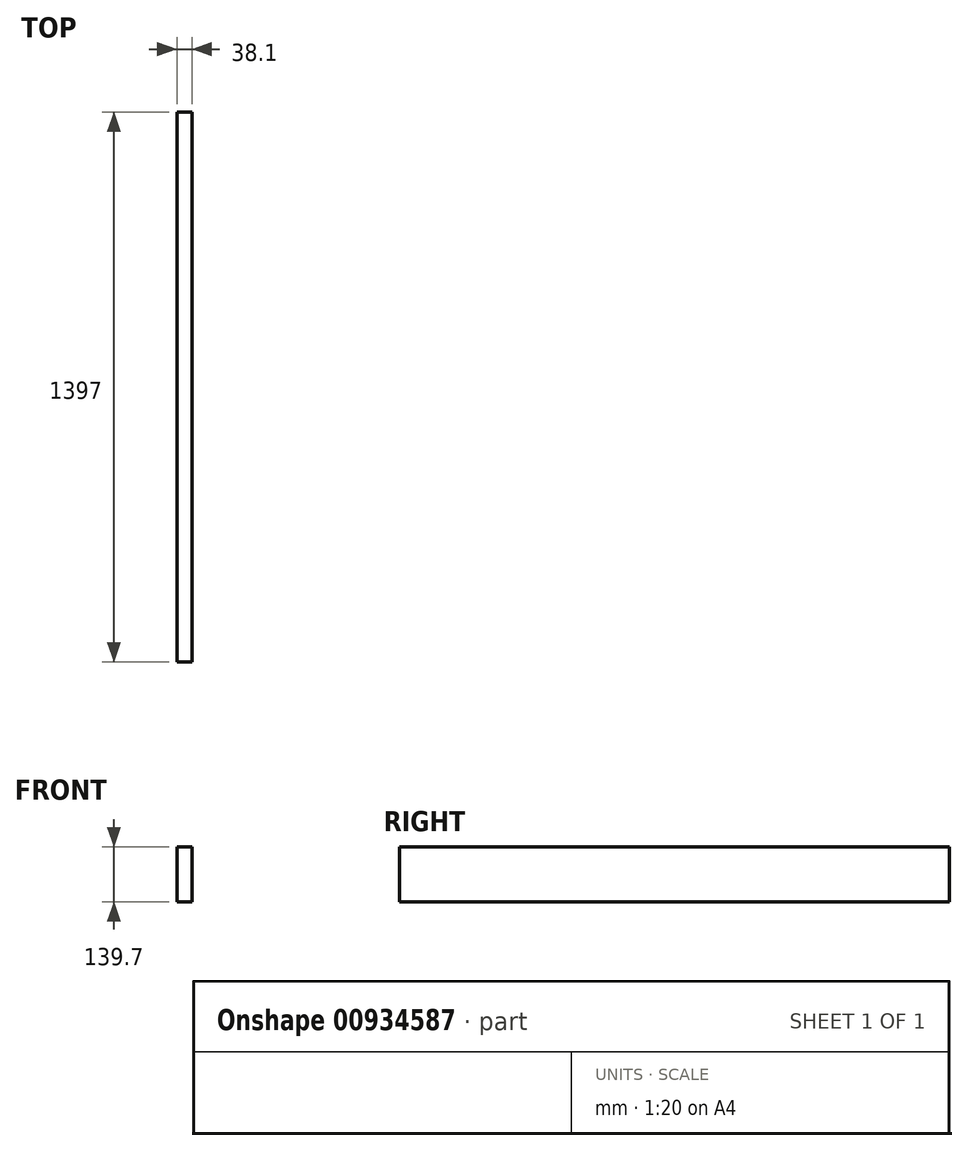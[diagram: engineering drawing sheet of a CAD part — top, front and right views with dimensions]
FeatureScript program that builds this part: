
annotation { "Feature Type Name" : "Feature", "Feature Type Description" : "" }
export const myFeature = defineFeature(function(context is Context, id is Id, definition is map)
    precondition{}
    {
        {
            var Q0;
            Q0=qCreatedBy(makeId("Front.planeOp"),FACE);
            var sketch = newSketch(context, id + "F0", { "sketchPlane" : qUnion([Q0])});
            skLineSegment(sketch, "E0.bottom", {"start": v(2386.69, -424.66) * mm, "end": v(2348.59, -424.66) * mm});
            skLineSegment(sketch, "E0.top", {"start": v(2386.69, -564.36) * mm, "end": v(2348.59, -564.36) * mm});
            skLineSegment(sketch, "E0.left", {"start": v(2386.69, -424.66) * mm, "end": v(2386.69, -564.36) * mm});
            skLineSegment(sketch, "E0.right", {"start": v(2348.59, -424.66) * mm, "end": v(2348.59, -564.36) * mm});
            skSolve(sketch);
        }
        {
            var Q0;
            Q0=makeQuery(id+"F0.imprint","IMPRINT",FACE,{"disambiguationData":[TD([[makeQuery(id+"F0.imprint","IMPRINT",EDGE,{"derivedFrom":sQuery(id+"F0.wireOp",EDGE,"E0.bottom")}),1.0]])]});
            extrude(context, id + "F1", {"entities" : qUnion([Q0]), "depth" : 1397 * mm, "offsetDistance" : 25.4 * mm});
        }
    });
